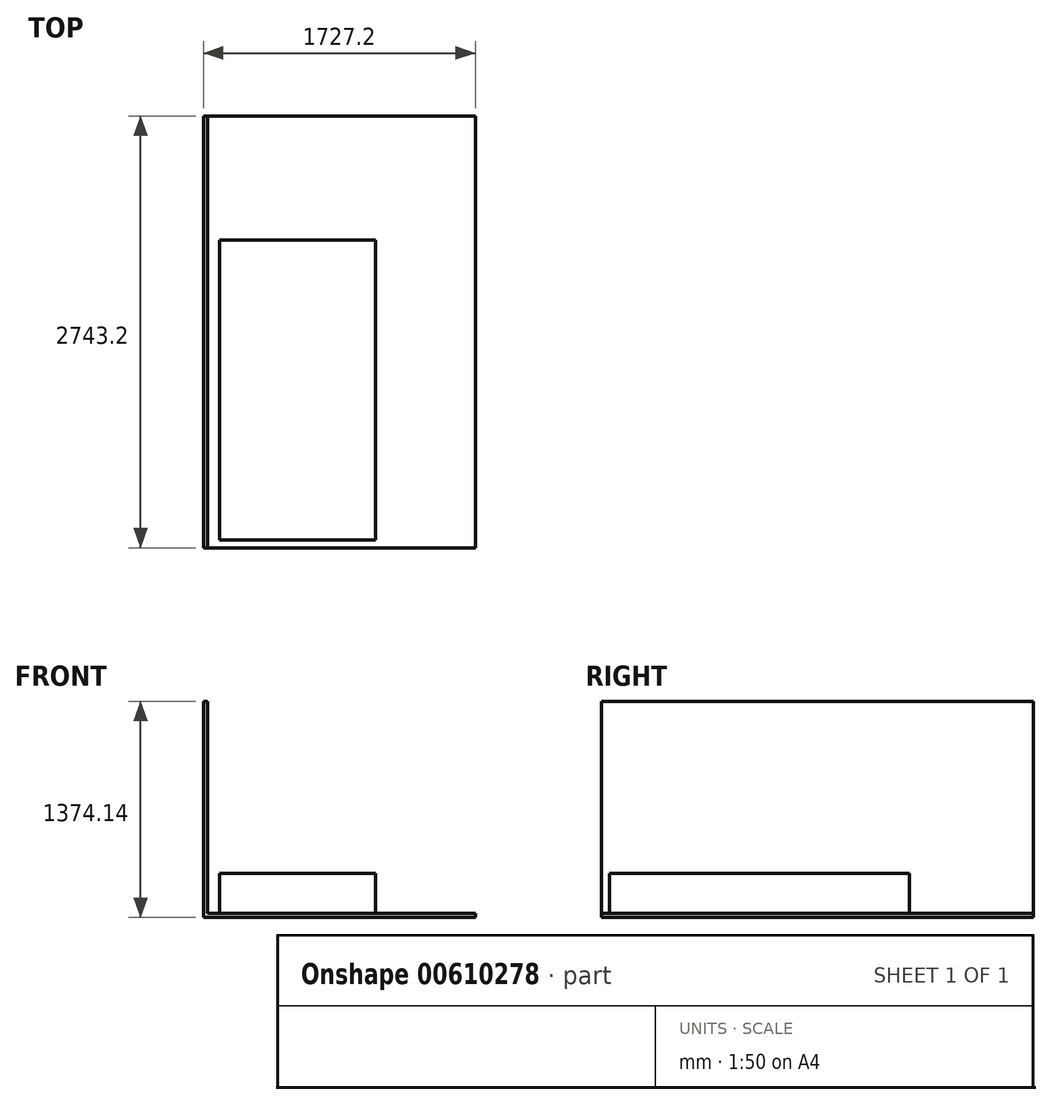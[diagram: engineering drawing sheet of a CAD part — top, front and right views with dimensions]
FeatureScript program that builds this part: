
annotation { "Feature Type Name" : "Feature", "Feature Type Description" : "" }
export const myFeature = defineFeature(function(context is Context, id is Id, definition is map)
    precondition{}
    {
        {
            var Q0;
            Q0=qCreatedBy(makeId("Top.planeOp"),FACE);
            var sketch = newSketch(context, id + "F0", { "sketchPlane" : qUnion([Q0])});
            skLineSegment(sketch, "E0.bottom", {"start": v(-850.9, 0) * mm, "end": v(0, 0) * mm});
            skLineSegment(sketch, "E0.top", {"start": v(-850.9, 2743.2) * mm, "end": v(0, 2743.2) * mm});
            skLineSegment(sketch, "E0.left", {"start": v(-850.9, 0) * mm, "end": v(-850.9, 2743.2) * mm});
            skLineSegment(sketch, "E0.right", {"start": v(0, 0) * mm, "end": v(0, 2743.2) * mm, "construction": true});
            skLineSegment(sketch, "E1.MirrorCS", {"start": v(850.9, 0) * mm, "end": v(0, 0) * mm});
            skLineSegment(sketch, "E2.MirrorCS", {"start": v(850.9, 0) * mm, "end": v(850.9, 2743.2) * mm});
            skLineSegment(sketch, "E3.MirrorCS", {"start": v(850.9, 2743.2) * mm, "end": v(0, 2743.2) * mm});
            skSolve(sketch);
        }
        {
            var Q0;
            Q0 = qSketchRegion(id + "F0", true);
            extrude(context, id + "F1", {"entities" : qUnion([Q0]), "oppositeDirection" : true, "depth" : 25.4 * mm, "offsetDistance" : 25.4 * mm});
        }
        {
            var Q0;
            Q0=makeQuery(id+"F1.opExtrude","SWEPT_FACE",FACE,{"disambiguationData":[OSD([sQuery(id+"F0.wireOp",EDGE,"E0.left")])]});
            var sketch = newSketch(context, id + "F2", { "sketchPlane" : qUnion([Q0])});
            skLineSegment(sketch, "E4.bottom", {"start": v(-2743.2, 0) * mm, "end": v(0, 0) * mm, "construction": true});
            skLineSegment(sketch, "E4.top", {"start": v(-2743.2, 1348.74) * mm, "end": v(0, 1348.74) * mm});
            skLineSegment(sketch, "E4.left", {"start": v(-2743.2, 0) * mm, "end": v(-2743.2, 1348.74) * mm});
            skLineSegment(sketch, "E4.right", {"start": v(0, 0) * mm, "end": v(0, 1348.74) * mm});
            skLineSegment(sketch, "E5", {"start": v(-2743.2, 0) * mm, "end": v(-2743.2, -25.4) * mm});
            skLineSegment(sketch, "E6", {"start": v(-2743.2, -25.4) * mm, "end": v(0, -25.4) * mm});
            skLineSegment(sketch, "E7", {"start": v(0, -25.4) * mm, "end": v(0, 0) * mm});
            skSolve(sketch);
        }
        {
            var Q0;
            Q0=makeQuery(id+"F2.imprint","IMPRINT",FACE,{"disambiguationData":[TD([[makeQuery(id+"F2.imprint","IMPRINT",EDGE,{"derivedFrom":sQuery(id+"F2.wireOp",EDGE,"E4.top")}),-1.0]])]});
            var Q1;
            Q1=makeQuery(id+"F2.imprint","IMPRINT",FACE,{"disambiguationData":[TD([[makeQuery(id+"F2.imprint","IMPRINT",EDGE,{"derivedFrom":sQuery(id+"F2.wireOp",EDGE,"E5")}),-1.0]])]});
            extrude(context, id + "F3", {"entities" : qUnion([Q0, Q1]), "operationType" : NewBodyOperationType.ADD, "depth" : 25.4 * mm, "offsetDistance" : 25.4 * mm});
        }
        {
            var Q0;
            Q0=makeQuery(id+"F1.opExtrude","CAP_FACE",FACE,{"disambiguationData":[OSD([sQuery(id+"F0.wireOp",EDGE,"E0.bottom"),sQuery(id+"F0.wireOp",EDGE,"E0.top"),sQuery(id+"F0.wireOp",EDGE,"E0.left"),sQuery(id+"F0.wireOp",EDGE,"E1.MirrorCS"),sQuery(id+"F0.wireOp",EDGE,"E2.MirrorCS"),sQuery(id+"F0.wireOp",EDGE,"E3.MirrorCS")])],"isStart":true});
            var sketch = newSketch(context, id + "F4", { "sketchPlane" : qUnion([Q0])});
            skLineSegment(sketch, "E8.bottom", {"start": v(-774.7, 50.8) * mm, "end": v(215.9, 50.8) * mm});
            skLineSegment(sketch, "E8.top", {"start": v(-774.7, 1955.8) * mm, "end": v(215.9, 1955.8) * mm});
            skLineSegment(sketch, "E8.left", {"start": v(-774.7, 50.8) * mm, "end": v(-774.7, 1955.8) * mm});
            skLineSegment(sketch, "E8.right", {"start": v(215.9, 50.8) * mm, "end": v(215.9, 1955.8) * mm});
            skSolve(sketch);
        }
        {
            var Q0;
            Q0 = qSketchRegion(id + "F4", true);
            extrude(context, id + "F5", {"entities" : qUnion([Q0]), "depth" : 254 * mm, "offsetDistance" : 25.4 * mm});
        }
    });
